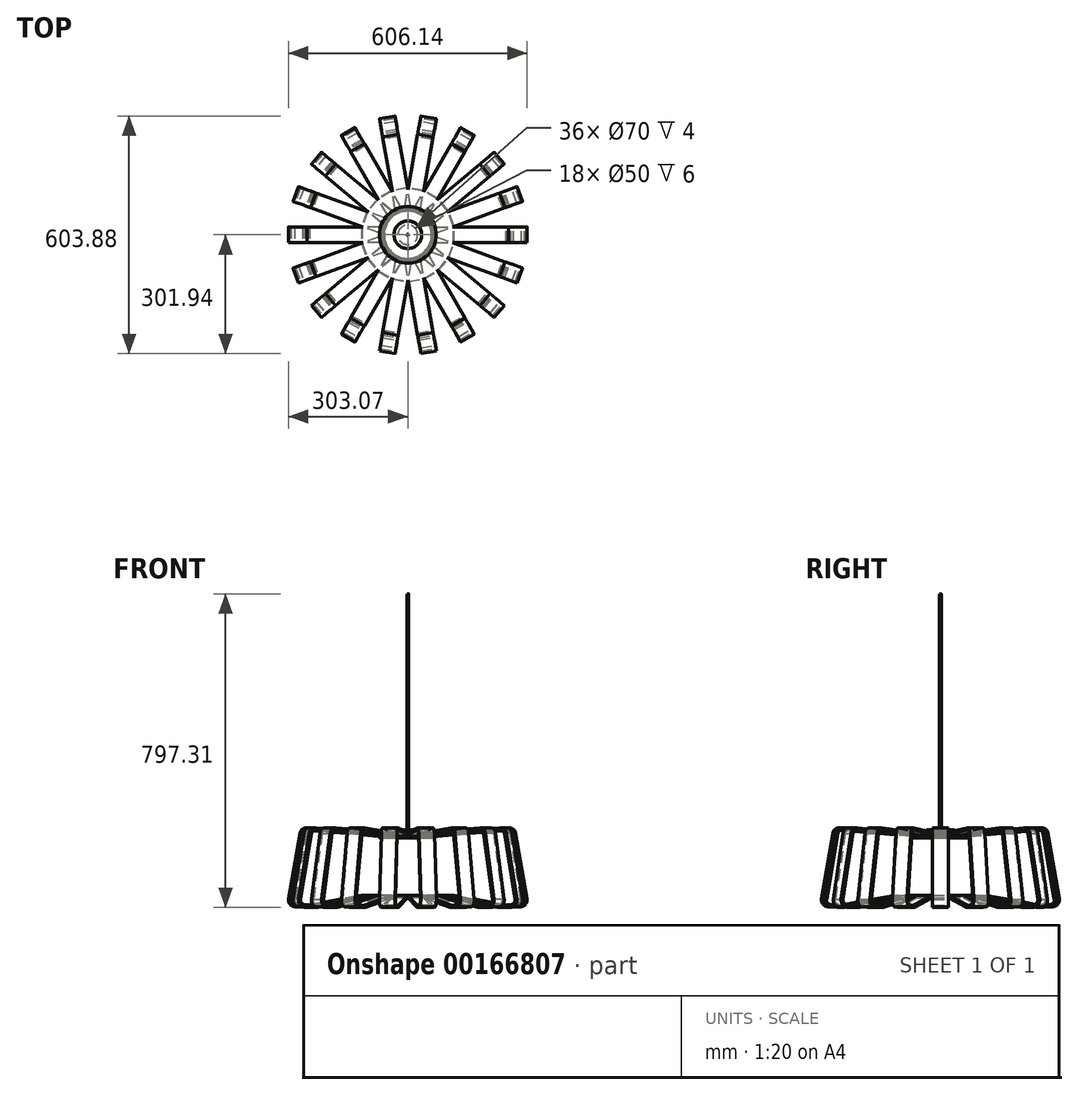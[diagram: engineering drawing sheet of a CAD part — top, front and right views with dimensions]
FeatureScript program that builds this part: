
annotation { "Feature Type Name" : "Feature", "Feature Type Description" : "" }
export const myFeature = defineFeature(function(context is Context, id is Id, definition is map)
    precondition{}
    {
        {
            var Q0;
            Q0=qCreatedBy(makeId("Front.planeOp"),FACE);
            var sketch = newSketch(context, id + "F0", { "sketchPlane" : qUnion([Q0])});
            skLineSegment(sketch, "E0", {"start": v(60, 0) * mm, "end": v(60, -6) * mm});
            skLineSegment(sketch, "E1", {"start": v(60, -6) * mm, "end": v(72, -6) * mm});
            skLineSegment(sketch, "E2", {"start": v(117.7, -156.64) * mm, "end": v(116.63, -162.54) * mm});
            skLineSegment(sketch, "E3", {"start": v(60, 0) * mm, "end": v(64, 0) * mm});
            skLineSegment(sketch, "E4", {"start": v(65.46, 0) * mm, "end": v(71.46, -0.02) * mm});
            skLineSegment(sketch, "E5", {"start": v(63.66, -2) * mm, "end": v(65.26, -2) * mm});
            skLineSegment(sketch, "E6", {"start": v(65.46, 0) * mm, "end": v(65.26, -2) * mm});
            skLineSegment(sketch, "E7", {"start": v(63.66, -2) * mm, "end": v(64, 0) * mm});
            skLineSegment(sketch, "E8", {"start": v(71.46, -0.02) * mm, "end": v(255.82, 15.36) * mm});
            skArc(sketch, "E9", {"start": v(273.98, 1.7) * mm, "mid": v(267.63, 12.15) * mm, "end": v(255.82, 15.36) * mm});
            skLineSegment(sketch, "E10", {"start": v(72, -6) * mm, "end": v(256.84, 9.42) * mm});
            skArc(sketch, "E11", {"start": v(267.98, 1.2) * mm, "mid": v(263.96, 7.4) * mm, "end": v(256.84, 9.42) * mm});
            skLineSegment(sketch, "E12", {"start": v(273.98, 1.7) * mm, "end": v(302.83, -165.84) * mm});
            skLineSegment(sketch, "E13", {"start": v(267.98, 1.2) * mm, "end": v(296.83, -166.34) * mm});
            skArc(sketch, "E14", {"start": v(287.43, -179.24) * mm, "mid": v(295.1, -174.95) * mm, "end": v(296.83, -166.34) * mm});
            skArc(sketch, "E15", {"start": v(288.43, -185.04) * mm, "mid": v(299.77, -178.54) * mm, "end": v(302.83, -165.84) * mm});
            skLineSegment(sketch, "E16", {"start": v(117.7, -156.64) * mm, "end": v(250.55, -180.62) * mm});
            skLineSegment(sketch, "E17", {"start": v(287.43, -179.24) * mm, "end": v(262.51, -181.32) * mm});
            skArc(sketch, "E18", {"start": v(250.55, -180.62) * mm, "mid": v(256.51, -181.33) * mm, "end": v(262.51, -181.32) * mm});
            skLineSegment(sketch, "E19", {"start": v(116.63, -162.54) * mm, "end": v(249.48, -186.52) * mm});
            skLineSegment(sketch, "E20", {"start": v(288.43, -185.04) * mm, "end": v(263.51, -187.12) * mm});
            skArc(sketch, "E21", {"start": v(249.48, -186.52) * mm, "mid": v(256.48, -187.26) * mm, "end": v(263.51, -187.12) * mm});
            skSolve(sketch);
        }
        {
            var Q0;
            Q0 = qSketchRegion(id + "F0", true);
            extrude(context, id + "F1", {"entities" : qUnion([Q0]), "endBound" : BoundingType.SYMMETRIC, "depth" : 40 * mm});
        }
        {
            var Q0;
            Q0=qCreatedBy(makeId("Front.planeOp"),FACE);
            var sketch = newSketch(context, id + "F2", { "sketchPlane" : qUnion([Q0])});
            skLineSegment(sketch, "E22", {"start": v(0, -83.1) * mm, "end": v(0, 87.88) * mm, "construction": true});
            skSolve(sketch);
        }
        {
            var Q0;
            Q0=qCreatedBy(makeId("Front.planeOp"),FACE);
            var sketch = newSketch(context, id + "F3", { "sketchPlane" : qUnion([Q0])});
            skLineSegment(sketch, "E23", {"start": v(72, -10) * mm, "end": v(72, -6.1) * mm});
            skLineSegment(sketch, "E24", {"start": v(72, 4) * mm, "end": v(72, 0.1) * mm});
            skLineSegment(sketch, "E25", {"start": v(72, -6.1) * mm, "end": v(59.9, -6.1) * mm});
            skLineSegment(sketch, "E26", {"start": v(59.9, -6.1) * mm, "end": v(59.9, 0.1) * mm});
            skLineSegment(sketch, "E27", {"start": v(59.9, 0.1) * mm, "end": v(64.15, 0.1) * mm});
            skLineSegment(sketch, "E28", {"start": v(72, 0.1) * mm, "end": v(65.85, 0.1) * mm});
            skLineSegment(sketch, "E29", {"start": v(65.65, -1.88) * mm, "end": v(64.37, -1.88) * mm});
            skLineSegment(sketch, "E30", {"start": v(64.15, 0.1) * mm, "end": v(64.37, -1.88) * mm});
            skLineSegment(sketch, "E31", {"start": v(65.85, 0.1) * mm, "end": v(65.65, -1.88) * mm});
            skLineSegment(sketch, "E32", {"start": v(72, 4) * mm, "end": v(35, 4) * mm});
            skLineSegment(sketch, "E33", {"start": v(35, 4) * mm, "end": v(35, 0) * mm});
            skLineSegment(sketch, "E34", {"start": v(35, 0) * mm, "end": v(25, 0) * mm});
            skLineSegment(sketch, "E35", {"start": v(25, 0) * mm, "end": v(25, -6) * mm});
            skLineSegment(sketch, "E36", {"start": v(25, -6) * mm, "end": v(35, -6) * mm});
            skLineSegment(sketch, "E37", {"start": v(35, -6) * mm, "end": v(35, -10) * mm});
            skLineSegment(sketch, "E38", {"start": v(35, -10) * mm, "end": v(72, -10) * mm});
            skSolve(sketch);
        }
        {
            var Q0;
            Q0 = qSketchRegion(id + "F3", true);
            var Q1;
            Q1=sQuery(id+"F2.wireOp",EDGE,"E22");
            revolve(context, id + "F4", {"operationType" : NewBodyOperationType.ADD, "entities" : qUnion([Q0]), "axis" : qUnion([Q1]), "revolveType" : RevolveType.FULL});
        }
        {
            var Q0;
            Q0=makeQuery(id+"F1.opExtrude","SWEPT_BODY",BODY,{"disambiguationData":[OSD([sQuery(id+"F0.wireOp",EDGE,"EnPrQVJO-aM4J-xbO5-wP3k-xNDsQ0UNJjnA"),sQuery(id+"F0.wireOp",EDGE,"SfafE3qQ-d5vd-lb26-k3x7-TeDYdtiUqBOX"),sQuery(id+"F0.wireOp",EDGE,"gFbipNy2-wf9R-PWlk-68pv-hQmzcTpnHxoE"),sQuery(id+"F0.wireOp",EDGE,"zUxbsKq2-lIy6-lC8s-67Ky-5WTl7rueX5Ys"),sQuery(id+"F0.wireOp",EDGE,"gDLolkIj-6pgt-coCG-UeOy-PtMzAoWhUuny"),sQuery(id+"F0.wireOp",EDGE,"E0"),sQuery(id+"F0.wireOp",EDGE,"E1"),sQuery(id+"F0.wireOp",EDGE,"GqueNZ4A-Kplb-cyow-Ig7x-FYeyt1Jr3gVC"),sQuery(id+"F0.wireOp",EDGE,"xrcsZSvc-bc5m-LqhF-PQ1e-80uCMXRr9TZD"),sQuery(id+"F0.wireOp",EDGE,"ZOsGsk9S-GZ5u-lRwm-dG85-1fZuS0bl3nWH"),sQuery(id+"F0.wireOp",EDGE,"E2"),sQuery(id+"F0.wireOp",EDGE,"Ag8UcAJj-w6Vf-UHbd-jnD7-DLcz9ZTILSw9")])]});
            var Q1;
            Q1=sQuery(id+"F2.wireOp",EDGE,"E22");
            circularPattern(context, id + "F5", {"entities" : qUnion([Q0]), "axis" : qUnion([Q1]), "angle" : 20 * degree, "instanceCount" : 18});
        }
        {
            var Q0;
            Q0=qCreatedBy(makeId("Front.planeOp"),FACE);
            var sketch = newSketch(context, id + "F6", { "sketchPlane" : qUnion([Q0])});
            skLineSegment(sketch, "E39", {"start": v(0, 0) * mm, "end": v(35, 0) * mm});
            skLineSegment(sketch, "E40", {"start": v(35, 0) * mm, "end": v(35, 10) * mm});
            skLineSegment(sketch, "E41", {"start": v(35, 10) * mm, "end": v(2, 10) * mm});
            skLineSegment(sketch, "E42", {"start": v(2, 10) * mm, "end": v(2, 610) * mm});
            skLineSegment(sketch, "E43", {"start": v(2, 610) * mm, "end": v(0, 610) * mm});
            skLineSegment(sketch, "E44", {"start": v(0, 610) * mm, "end": v(0, 0) * mm});
            skSolve(sketch);
        }
        {
            var Q0;
            Q0=qCreatedBy(makeId("Front.planeOp"),FACE);
            var sketch = newSketch(context, id + "F7", { "sketchPlane" : qUnion([Q0])});
            skLineSegment(sketch, "E45", {"start": v(0, -34.56) * mm, "end": v(0, 665.44) * mm, "construction": true});
            skSolve(sketch);
        }
        {
            var Q0;
            Q0 = qSketchRegion(id + "F6", true);
            var Q1;
            Q1 = qConstructionFilter(qBodyType(qCreatedBy(id + "F6" ,EDGE), BodyType.WIRE), ConstructionObject.NO);
            var Q2;
            Q2=sQuery(id+"F7.wireOp",EDGE,"E45");
            revolve(context, id + "F8", {"entities" : qUnion([Q0]), "surfaceEntities" : qUnion([Q1]), "axis" : qUnion([Q2]), "revolveType" : RevolveType.FULL});
        }
    });
